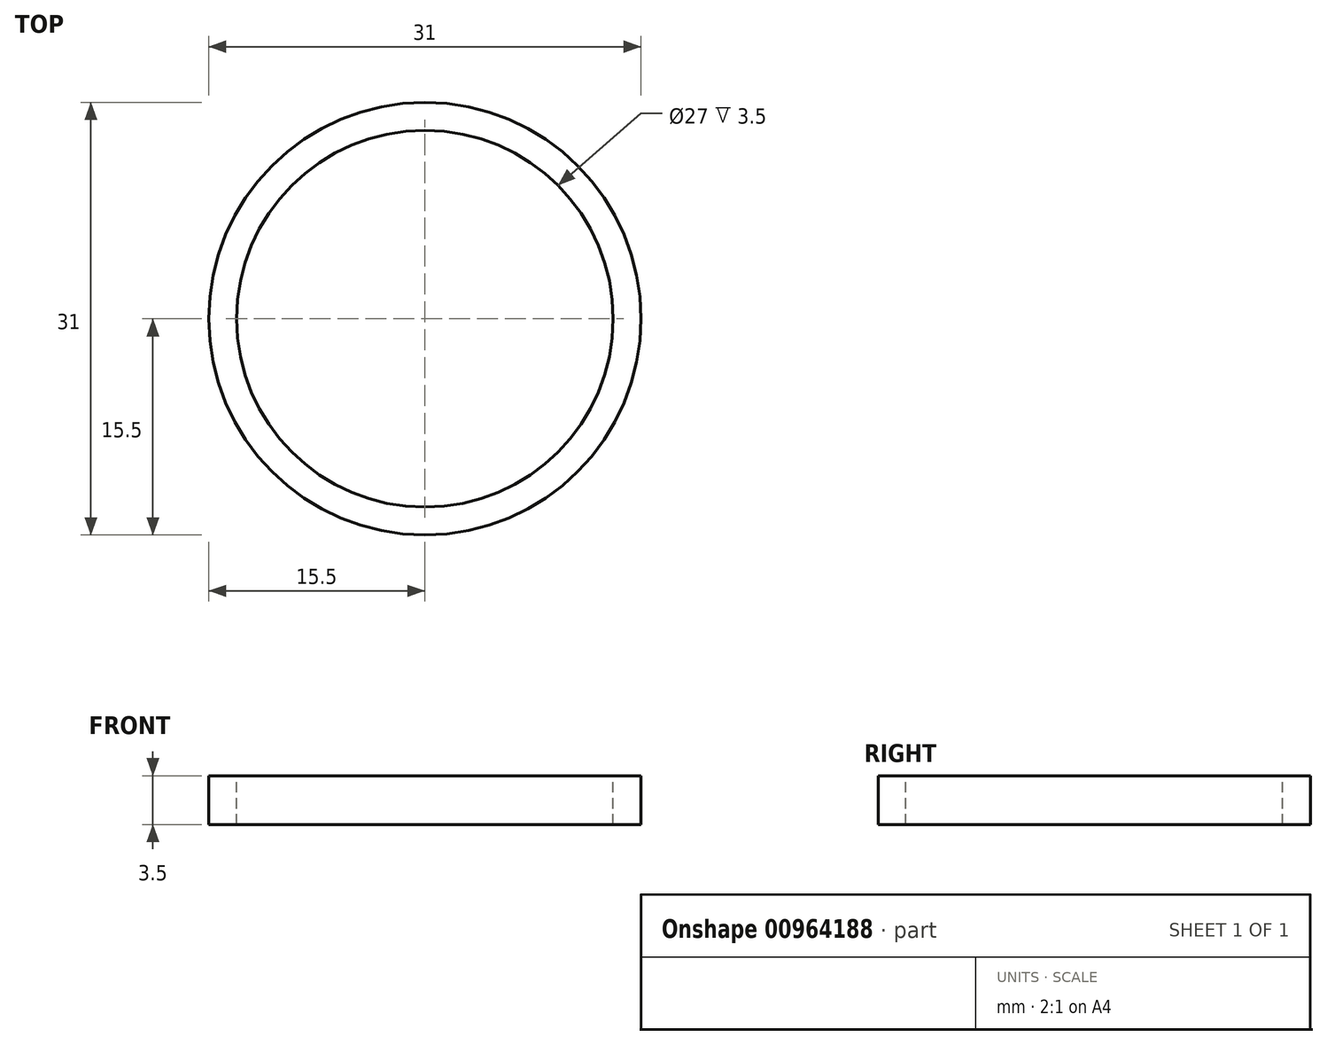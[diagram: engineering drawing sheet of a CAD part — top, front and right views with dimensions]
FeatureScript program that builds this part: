
annotation { "Feature Type Name" : "Feature", "Feature Type Description" : "" }
export const myFeature = defineFeature(function(context is Context, id is Id, definition is map)
    precondition{}
    {
        {
            var Q0;
            Q0=qCreatedBy(makeId("Top.planeOp"),FACE);
            var sketch = newSketch(context, id + "F0", { "sketchPlane" : qUnion([Q0])});
            skCircle(sketch, "E0", {"center": v(0, 0) * mm, "radius": 15.5 * mm});
            skSolve(sketch);
        }
        {
            var Q0;
            Q0 = qSketchRegion(id + "F0", true);
            extrude(context, id + "F1", {"entities" : qUnion([Q0]), "depth" : 3.5 * mm, "offsetDistance" : 25 * mm});
        }
        {
            var Q0;
            Q0=makeQuery(id+"F1.opExtrude","CAP_FACE",FACE,{"disambiguationData":[OSD([sQuery(id+"F0.wireOp",EDGE,"E0")])],"isStart":false});
            var sketch = newSketch(context, id + "F2", { "sketchPlane" : qUnion([Q0])});
            skCircle(sketch, "E1.0", {"center": v(0, 0) * mm, "radius": 13.5 * mm});
            skSolve(sketch);
        }
        {
            var Q0;
            Q0 = qSketchRegion(id + "F2", true);
            var Q1;
            Q1=makeQuery(id+"F1.opExtrude","CAP_FACE",FACE,{"disambiguationData":[OSD([sQuery(id+"F0.wireOp",EDGE,"E0")])],"isStart":true});
            extrude(context, id + "F3", {"entities" : qUnion([Q0]), "operationType" : NewBodyOperationType.REMOVE, "endBound" : BoundingType.UP_TO_SURFACE, "oppositeDirection" : true, "depth" : 25 * mm, "endBoundEntityFace" : qUnion([Q1]), "offsetDistance" : 25 * mm});
        }
    });
